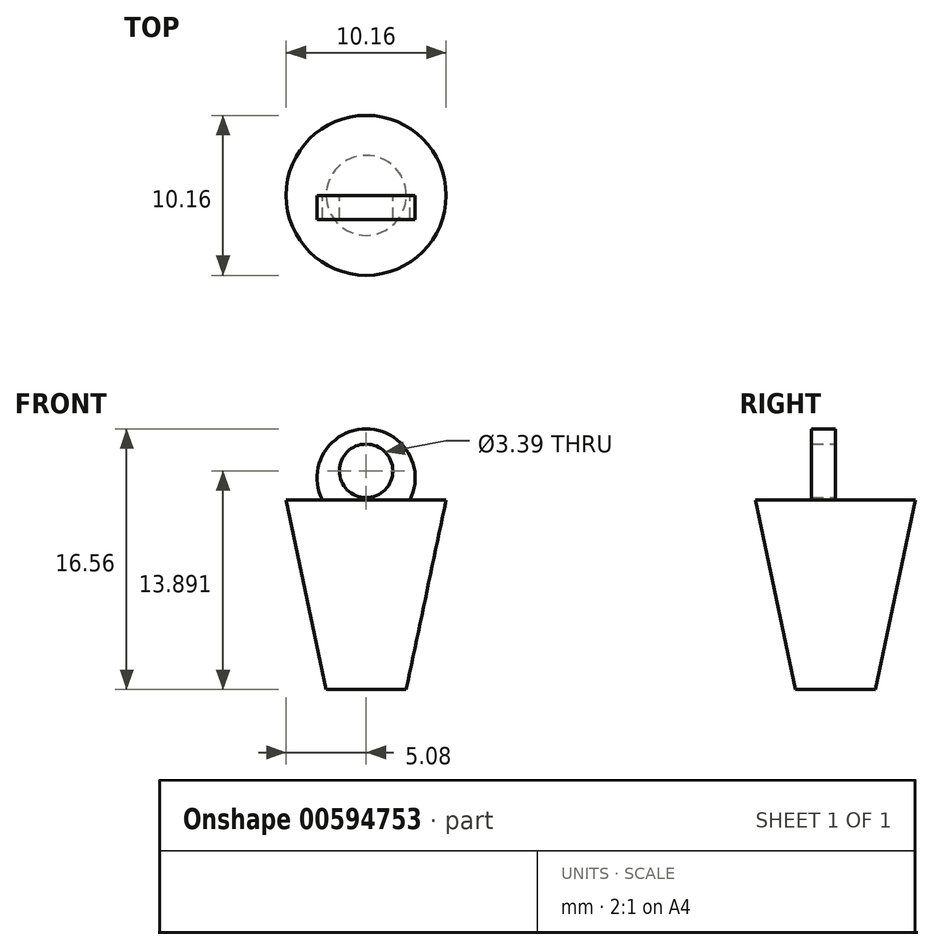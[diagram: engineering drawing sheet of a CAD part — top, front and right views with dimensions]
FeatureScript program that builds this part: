
annotation { "Feature Type Name" : "Feature", "Feature Type Description" : "" }
export const myFeature = defineFeature(function(context is Context, id is Id, definition is map)
    precondition{}
    {
        {
            var Q0;
            Q0=qCreatedBy(makeId("Front.planeOp"),FACE);
            var sketch = newSketch(context, id + "F0", { "sketchPlane" : qUnion([Q0])});
            skLineSegment(sketch, "E0", {"start": v(0, 0) * mm, "end": v(-2.54, 0) * mm});
            skLineSegment(sketch, "E1", {"start": v(-2.54, 0) * mm, "end": v(-5.08, 12.03) * mm});
            skLineSegment(sketch, "E2", {"start": v(-5.08, 12.03) * mm, "end": v(0, 12.03) * mm});
            skLineSegment(sketch, "E3", {"start": v(0, 12.03) * mm, "end": v(0, 0) * mm});
            skSolve(sketch);
        }
        {
            var Q0;
            Q0=makeQuery(id+"F0.imprint","IMPRINT",FACE,{"disambiguationData":[TD([[makeQuery(id+"F0.imprint","IMPRINT",EDGE,{"derivedFrom":sQuery(id+"F0.wireOp",EDGE,"E0")}),-1.0]])]});
            var Q1;
            Q1=sQuery(id+"F0.wireOp",EDGE,"E3");
            revolve(context, id + "F1", {"entities" : qUnion([Q0]), "axis" : qUnion([Q1]), "revolveType" : RevolveType.FULL});
        }
        {
            var Q0;
            Q0=qCreatedBy(makeId("Right.planeOp"),FACE);
            var sketch = newSketch(context, id + "F2", { "sketchPlane" : qUnion([Q0])});
            skCircle(sketch, "E4", {"center": v(0, 19.66) * mm, "radius": 0.06 * mm});
            skSolve(sketch);
        }
        {
            var Q0;
            Q0=makeQuery(id+"F2.imprint","IMPRINT",FACE,{"disambiguationData":[TD([[makeQuery(id+"F2.imprint","IMPRINT",EDGE,{"derivedFrom":sQuery(id+"F2.wireOp",EDGE,"E4")}),1.0]])]});
            extrude(context, id + "F3", {"entities" : qUnion([Q0]), "operationType" : NewBodyOperationType.REMOVE, "endBound" : BoundingType.SYMMETRIC, "oppositeDirection" : true, "depth" : 25.4 * mm, "offsetDistance" : 25.4 * mm});
        }
        {
            var Q0;
            Q0=qCreatedBy(makeId("Front.planeOp"),FACE);
            var sketch = newSketch(context, id + "F4", { "sketchPlane" : qUnion([Q0])});
            skCircle(sketch, "E5", {"center": v(0, 13.45) * mm, "radius": 3.11 * mm});
            skSolve(sketch);
        }
        {
            var Q0;
            Q0 = qSketchRegion(id + "F4", true);
            extrude(context, id + "F5", {"entities" : qUnion([Q0]), "operationType" : NewBodyOperationType.ADD, "depth" : 1.52 * mm, "offsetDistance" : 25.4 * mm});
        }
        {
            var Q0;
            Q0=qCreatedBy(makeId("Front.planeOp"),FACE);
            var sketch = newSketch(context, id + "F6", { "sketchPlane" : qUnion([Q0])});
            skCircle(sketch, "E6", {"center": v(0, 13.9) * mm, "radius": 1.7 * mm});
            skSolve(sketch);
        }
        {
            var Q0;
            Q0 = qSketchRegion(id + "F6", true);
            extrude(context, id + "F7", {"entities" : qUnion([Q0]), "operationType" : NewBodyOperationType.REMOVE, "depth" : 27.43 * mm, "offsetDistance" : 25.4 * mm});
        }
    });
